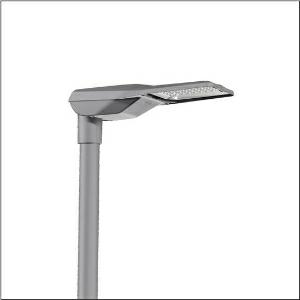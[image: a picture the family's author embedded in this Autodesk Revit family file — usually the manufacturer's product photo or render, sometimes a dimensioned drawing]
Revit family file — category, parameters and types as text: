
# Revit family: streetlight_sl_21_iq_mini___stw1_0a_5xe2e31g08gb_0d22
name_source: partatom
category: Lighting Fixtures
units: mm (PartAtom-declared; Revit-internal decimal feet)

## family parameters
Cut with Voids When Loaded = No
Host = Face
Light Source = No
Part Type = Normal
Room Calculation Point = No
Round Connector Dimension = Use Diameter
Shared = No

## types (1)
- --- (1 x LED, 5680 lm, 37.1 W, 3000K)
    Apparent Load = 37 VA
    CIE Flux Codes = 38 75 98 100 100
    Color Rendering = 70
    Color Temperature = 3000K
    Default Elevation = 1800 mm
    Description = Streetlight SL 21 iQ mini, mast luminaire, primary light control with lens, of PMMA, primary optical cover: cover, of toughened safety glass, transparent, light distribution: STW1.0a, light emission: direct distribution, primary light characteristic: asymmetric, installation type: post-top, side-entry, LED, High Power LED, rated luminous flux: 5.680lm, luminous efficacy: 153lm/W, light colour: 730, colour temperature: 3000K, control gear: iQ Street-Remote, control: Street-Remote, Auto-Match, Temp-Guard, Lumen-Switch, Night-Set, Smart-Wire, Light-Fading, Desk-Remote (wireless, voltage-free reading and setting of iQ features in the workshop via application-optimized NFC function/RFID function), optimised constant luminous flux control (CLO 2.0), pre-setting: linear dimming characteristic, mains connection: 220..240V, AC, 50/60Hz, start of lifetime: 37W, end of service life: 39W, reduction: 18W, luminaire housing, of diecast aluminium, powder-coated, SITECO metallic grey (DB 702S), corrosivity category C5 high according to DIN EN ISO 12944, please order mast flange separately, inclination adjustable: 0°, 5°, 10°, 15°, sealing non-destructively replaceable, multi-level sealing system, length: 628mm, width: 235mm, height: 110mm, mast flange for spigot size: 42mm (side-entry): 5XC10008XM4, 60/48mm (side-entry/post-top): 5XC10108XM2, 76/60mm (side-entry/post-top): 5XC10108XM1, mounting height: 4..8m, protection rating (complete): IP66, insulation class (complete): insulation class II (safety insulation), certification: CE, ENEC, ENEC+, VDE, impact resistance: IK10, permissible operating ambient temperature for outdoor applications: -40..+50°C, standard-compliant lighting for roads and squares, packaging unit: 1 piece

Light Distribution: STW1.0a
    Height = 110 mm
    Lamp = 1 x LED
    Lamp Light Flux = 5680 lm
    Lamp Power = 37.1 W
    Lamp count = 1
    Length = 625 mm
    Luminous efficacy = 153 lm/W
    Manufacturer = Siteco
    ModVariant = No
    Model = 5XE2E31G08GB
    Number of Poles = 1
    OnlyDefault = Yes
    Power Factor = 1
    Product Name = Streetlight SL 21 iQ mini | STW1.0a
    Product group = mast luminaire | pylon top
    ProductGroupID = 6100
    Protection Class = Protection class II
    Protection Degree = IP 66
    RLX_Detail_Level = 1
    RLX_Emergency_Light_Flux = 0 lm
    RLX_Emergency_Type = 0
    RLX_Emergency_Type_DB = No
    RlxData = <blob elided: 26405 chars, md5=a7c374fe>
    Socket = socket
    Standby Power = 0 W
    System Light Flux = 5680 lm
    System Power = 37 W
    Type Comments = factory setting: luminous flux: 100 % | dim-lin: 254 | 385 mA
    Type Image = l_1003519.jpg
    URL = http://relux.com
    VarID = @adj_185023
    Voltage = 0 V
    Weight = 0.00 kg
    Width = 234 mm

## geometry (parser evidence)
native form markers: Blend x4, Sweep x9
no freeform markers — native parametric forms only
